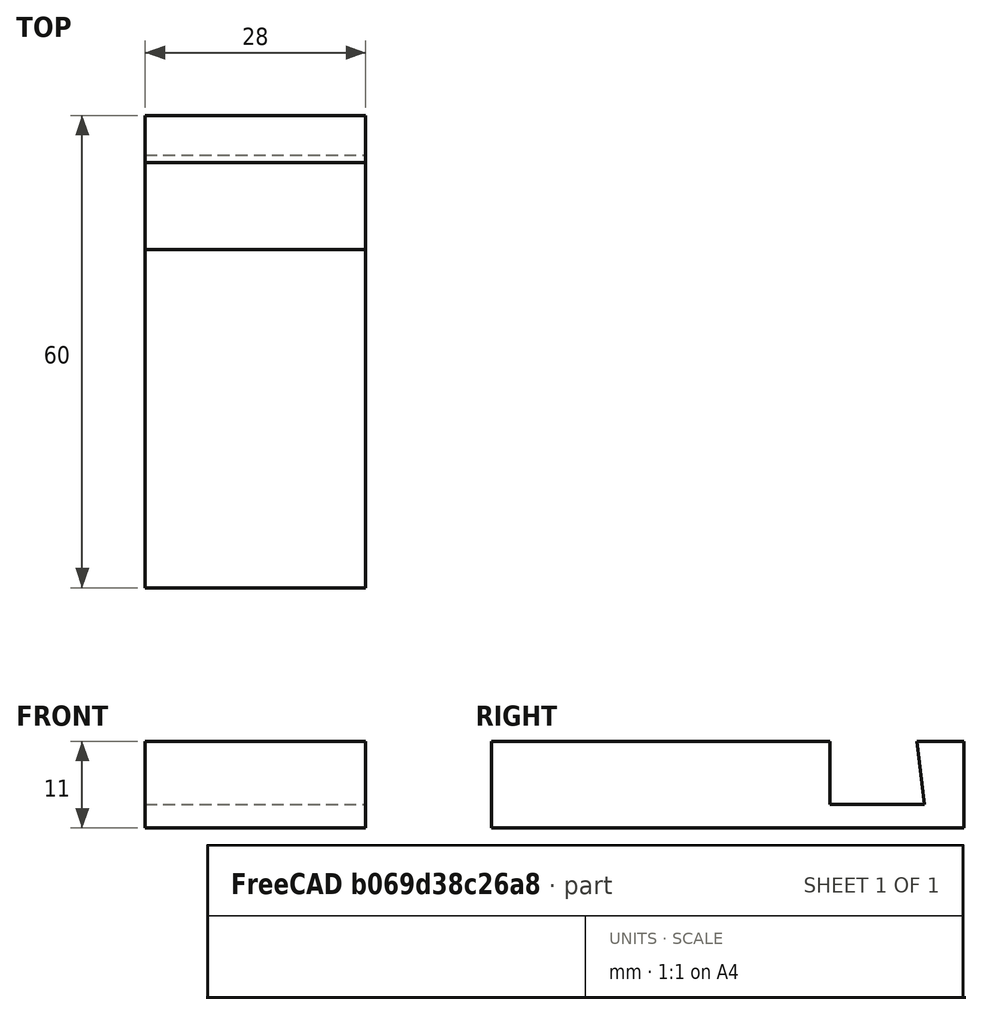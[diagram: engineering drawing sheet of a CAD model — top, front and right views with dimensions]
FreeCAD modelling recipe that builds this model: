
FCSTD DOCUMENT  (FreeCAD 0.16R6707 (Git))
Label: 04-porta-moviles
License: All rights reserved
LicenseURL: http://en.wikipedia.org/wiki/All_rights_reserved
objects: Sketcher::SketchObject×1, PartDesign::Pad×1
note: 3 computed .brp shape members not serialized (recipe doc carries the construction recipe); baked Part::Feature solids carry a one-line shape summary decoded from their .brp

FEATURE [Sketcher::SketchObject] Sketch
  Placement = pos=(0,0,0) rot=(0.57735,0.57735,0.57735;2.0944rad)
  sketch-geometry (8):
    g0: LineSegment StartX=0 StartY=11 StartZ=0 EndX=0 EndY=0 EndZ=0
    g1: LineSegment StartX=0 StartY=0 StartZ=0 EndX=60 EndY=0 EndZ=0
    g2: LineSegment StartX=60 StartY=0 StartZ=0 EndX=60 EndY=11 EndZ=0
    g3: LineSegment StartX=60 StartY=11 StartZ=0 EndX=54 EndY=11 EndZ=0
    g4: LineSegment StartX=54 StartY=11 StartZ=0 EndX=55 EndY=3 EndZ=0
    g5: LineSegment StartX=55 StartY=3 StartZ=0 EndX=43 EndY=3 EndZ=0
    g6: LineSegment StartX=43 StartY=3 StartZ=0 EndX=43 EndY=11 EndZ=0
    g7: LineSegment StartX=43 StartY=11 StartZ=0 EndX=0 EndY=11 EndZ=0
  constraints (23):
    c: Vertical(g0)
    c: Coincident(g0,g1)
    c: Horizontal(g1)
    c: Coincident(g1,g2)
    c: Coincident(g2,g3)
    c: Coincident(g3,g4)
    c: Coincident(g4,g5)
    c: Horizontal(g5)
    c: Coincident(g5,g6)
    c: Vertical(g6)
    c: Coincident(g6,g7)
    c: Coincident(g7,g0)
    c: Horizontal(g7)
    c: DistanceY(g0,g0) = 11
    c: DistanceX(g1,g1) = 60
    c: DistanceX(g6,g3) = 11
    c: Vertical(g2)
    c: Horizontal(g3)
    c: Equal(g2,g0)
    c: DistanceY(g1,g4) = 3
    c: DistanceX(g5,g5) = 12
    c: Coincident(g0,g-1)
    c: DistanceX(g3,g2) = 6
FEATURE [PartDesign::Pad] Pad
  Length = 28
  Length2 = 100
  Midplane = true
  Placement = pos=(0,0,0) rot=(0.57735,0.57735,0.57735;2.0944rad)
  Sketch = -> Sketch
  Type = 0
